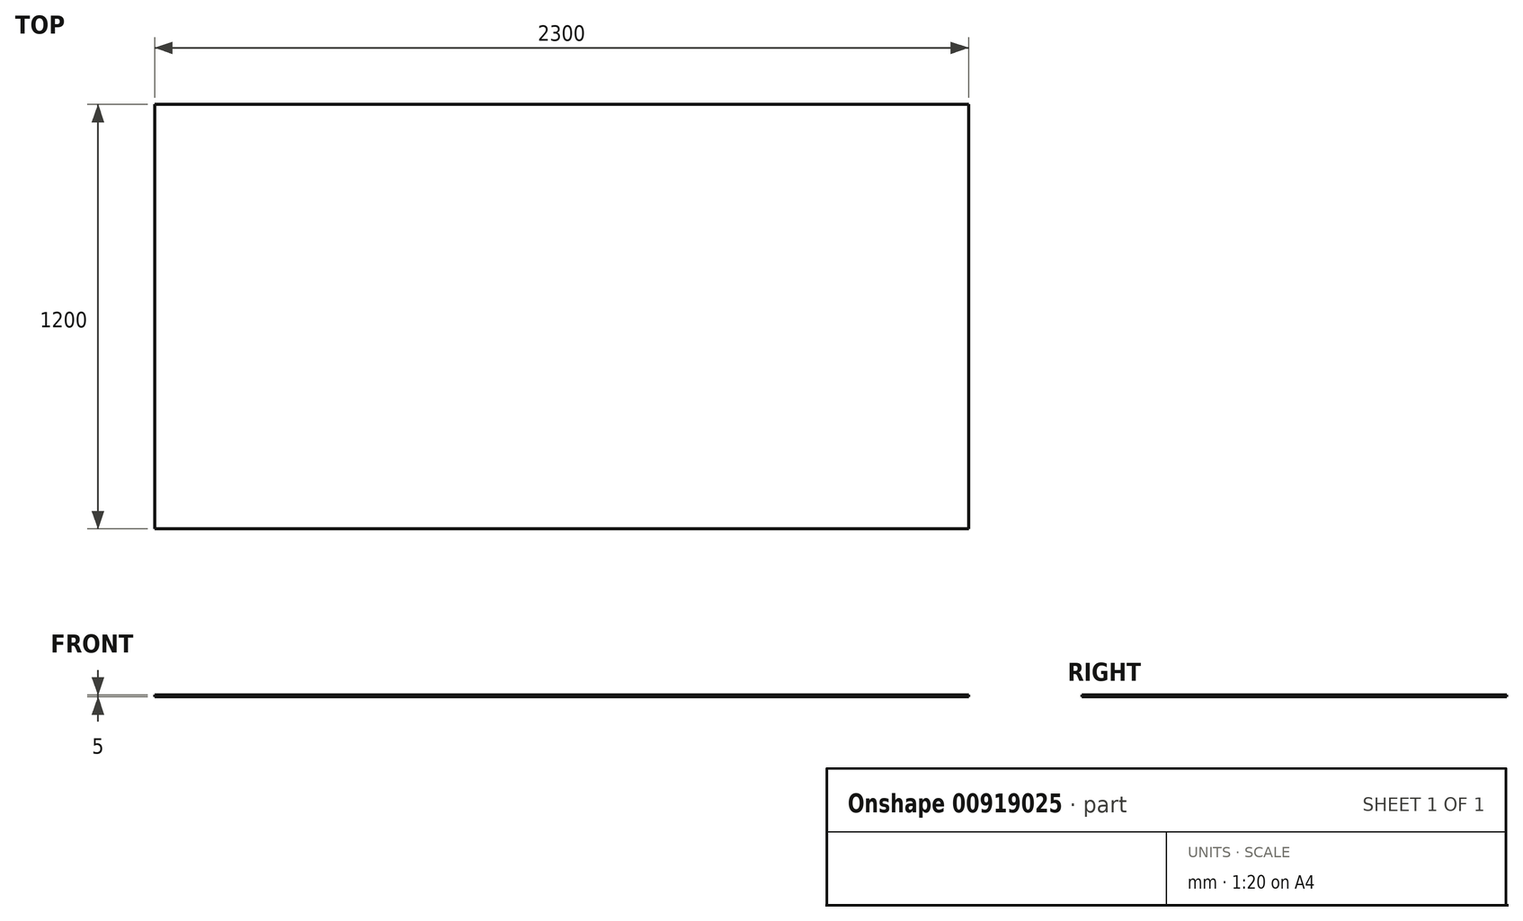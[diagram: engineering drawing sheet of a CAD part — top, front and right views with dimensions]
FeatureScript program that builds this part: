
annotation { "Feature Type Name" : "Feature", "Feature Type Description" : "" }
export const myFeature = defineFeature(function(context is Context, id is Id, definition is map)
    precondition{}
    {
        {
            var Q0;
            Q0=qCreatedBy(makeId("Top.planeOp"),FACE);
            var sketch = newSketch(context, id + "F0", { "sketchPlane" : qUnion([Q0])});
            skLineSegment(sketch, "E0.bottom", {"start": v(1150, 600) * mm, "end": v(-1150, 600) * mm});
            skLineSegment(sketch, "E0.top", {"start": v(1150, -600) * mm, "end": v(-1150, -600) * mm});
            skLineSegment(sketch, "E0.left", {"start": v(1150, 600) * mm, "end": v(1150, -600) * mm});
            skLineSegment(sketch, "E0.right", {"start": v(-1150, 600) * mm, "end": v(-1150, -600) * mm});
            skPoint(sketch, "E0.middle", {"position": v(0, 0) * mm});
            skSolve(sketch);
        }
        {
            var Q0;
            Q0=makeQuery(id+"F0.imprint","IMPRINT",FACE,{"disambiguationData":[TD([[makeQuery(id+"F0.imprint","IMPRINT",EDGE,{"derivedFrom":sQuery(id+"F0.wireOp",EDGE,"E0.bottom")}),1.0]])]});
            extrude(context, id + "F1", {"entities" : qUnion([Q0]), "oppositeDirection" : true, "depth" : 5 * mm, "offsetDistance" : 25 * mm});
        }
    });
